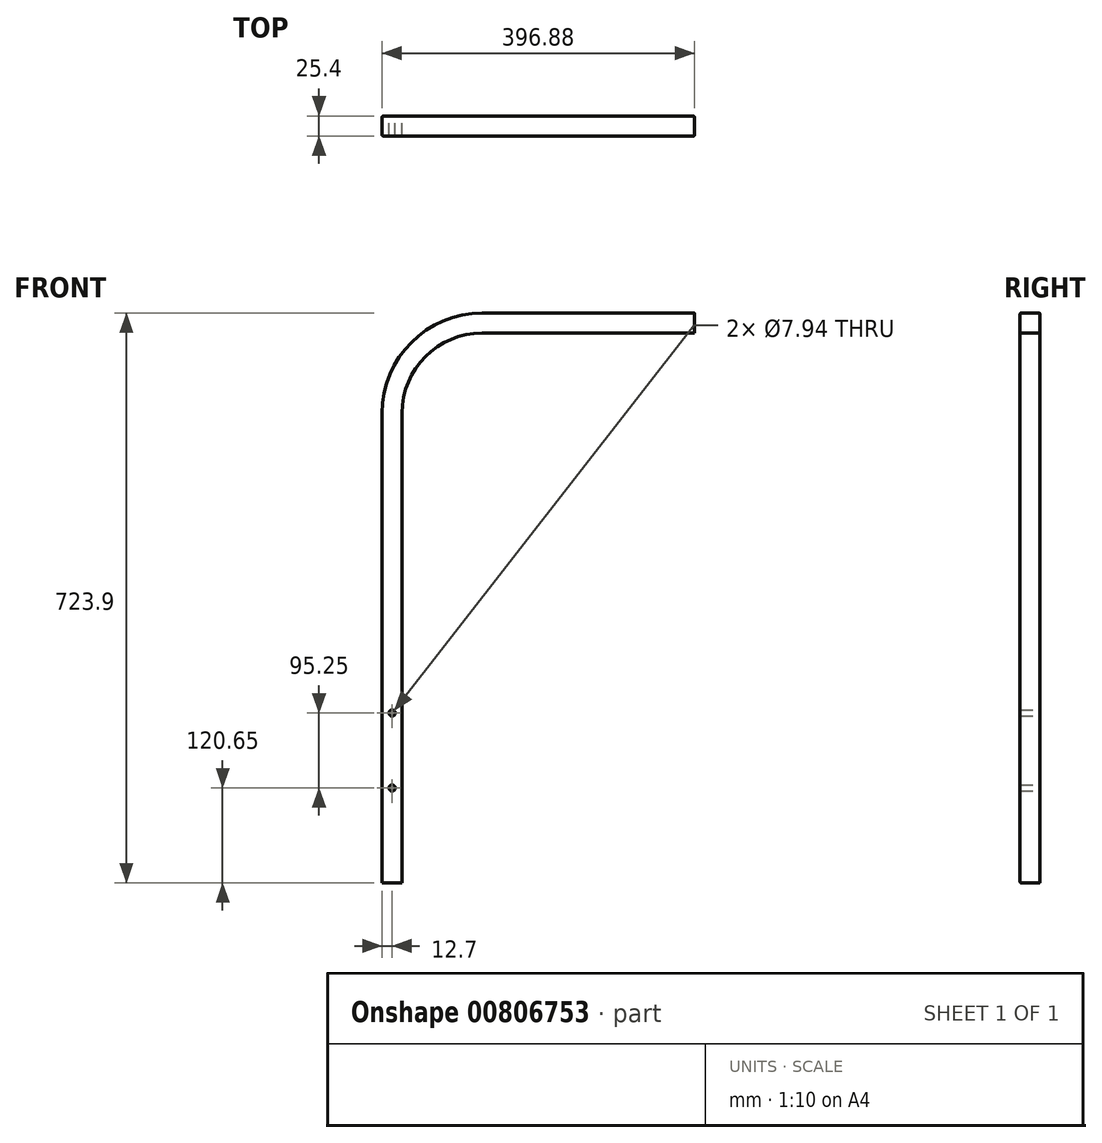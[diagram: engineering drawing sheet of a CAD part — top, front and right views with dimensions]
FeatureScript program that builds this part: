
annotation { "Feature Type Name" : "Feature", "Feature Type Description" : "" }
export const myFeature = defineFeature(function(context is Context, id is Id, definition is map)
    precondition{}
    {
        {
            var Q0;
            Q0=qCreatedBy(makeId("Front.planeOp"),FACE);
            var sketch = newSketch(context, id + "F0", { "sketchPlane" : qUnion([Q0])});
            skLineSegment(sketch, "E0", {"start": v(0, 0) * mm, "end": v(0, 596.9) * mm});
            skLineSegment(sketch, "E1", {"start": v(127, 723.9) * mm, "end": v(396.88, 723.9) * mm});
            skPoint(sketch, "E2.visualSharp", {"position": v(0, 723.9) * mm});
            skArc(sketch, "E2.filletArc", {"start": v(127, 723.9) * mm, "mid": v(37.2, 686.7) * mm, "end": v(0, 596.9) * mm});
            skLineSegment(sketch, "E3.0", {"start": v(25.4, 0) * mm, "end": v(25.4, 596.9) * mm});
            skArc(sketch, "E3.1", {"start": v(127, 698.5) * mm, "mid": v(55.16, 668.74) * mm, "end": v(25.4, 596.9) * mm});
            skLineSegment(sketch, "E3.2", {"start": v(127, 698.5) * mm, "end": v(396.88, 698.5) * mm});
            skLineSegment(sketch, "E4", {"start": v(396.88, 723.9) * mm, "end": v(396.88, 698.5) * mm});
            skLineSegment(sketch, "E5", {"start": v(25.4, 0) * mm, "end": v(0, 0) * mm});
            skCircle(sketch, "E6", {"center": v(12.7, 120.65) * mm, "radius": 3.97 * mm});
            skPoint(sketch, "E6.centerSnap0", {"position": v(12.7, 0) * mm});
            skCircle(sketch, "E7", {"center": v(12.7, 215.9) * mm, "radius": 3.97 * mm});
            skSolve(sketch);
        }
        {
            var Q0;
            Q0 = qSketchRegion(id + "F0", true);
            extrude(context, id + "F1", {"entities" : qUnion([Q0]), "depth" : 25.4 * mm, "offsetDistance" : 25.4 * mm});
        }
        {
            var Q0;
            Q0=makeQuery(id+"F1.opExtrude","CAP_EDGE",EDGE,{"disambiguationData":[OSD([sQuery(id+"F0.wireOp",EDGE,"E3.0")])],"isStart":false});
            var Q1;
            Q1=makeQuery(id+"F1.opExtrude","CAP_EDGE",EDGE,{"disambiguationData":[OSD([sQuery(id+"F0.wireOp",EDGE,"E0")])],"isStart":false});
            var Q2;
            Q2=makeQuery(id+"F1.opExtrude","CAP_EDGE",EDGE,{"disambiguationData":[OSD([sQuery(id+"F0.wireOp",EDGE,"E0")])],"isStart":true});
            var Q3;
            Q3=makeQuery(id+"F1.opExtrude","CAP_EDGE",EDGE,{"disambiguationData":[OSD([sQuery(id+"F0.wireOp",EDGE,"E3.0")])],"isStart":true});
            var Q4;
            Q4=makeQuery(id+"F1.opExtrude","CAP_FACE",FACE,{"disambiguationData":[OSD([sQuery(id+"F0.wireOp",EDGE,"E0"),sQuery(id+"F0.wireOp",EDGE,"E1"),sQuery(id+"F0.wireOp",EDGE,"E2.filletArc"),sQuery(id+"F0.wireOp",EDGE,"E3.0"),sQuery(id+"F0.wireOp",EDGE,"E3.1"),sQuery(id+"F0.wireOp",EDGE,"E3.2"),sQuery(id+"F0.wireOp",EDGE,"E4"),sQuery(id+"F0.wireOp",EDGE,"E5"),sQuery(id+"F0.wireOp",EDGE,"E6"),sQuery(id+"F0.wireOp",EDGE,"E7")])],"isStart":true});
            var Q5;
            Q5=makeQuery(id+"F1.opExtrude","CAP_FACE",FACE,{"disambiguationData":[OSD([sQuery(id+"F0.wireOp",EDGE,"E0"),sQuery(id+"F0.wireOp",EDGE,"E1"),sQuery(id+"F0.wireOp",EDGE,"E2.filletArc"),sQuery(id+"F0.wireOp",EDGE,"E3.0"),sQuery(id+"F0.wireOp",EDGE,"E3.1"),sQuery(id+"F0.wireOp",EDGE,"E3.2"),sQuery(id+"F0.wireOp",EDGE,"E4"),sQuery(id+"F0.wireOp",EDGE,"E5"),sQuery(id+"F0.wireOp",EDGE,"E6"),sQuery(id+"F0.wireOp",EDGE,"E7")])],"isStart":false});
            fillet(context, id + "F2", {"entities" : qUnion([Q0, Q1, Q2, Q3, Q4, Q5]), "radius" : 1.52 * mm, "tangentPropagation" : true, "allowEdgeOverflow" : false});
        }
    });
